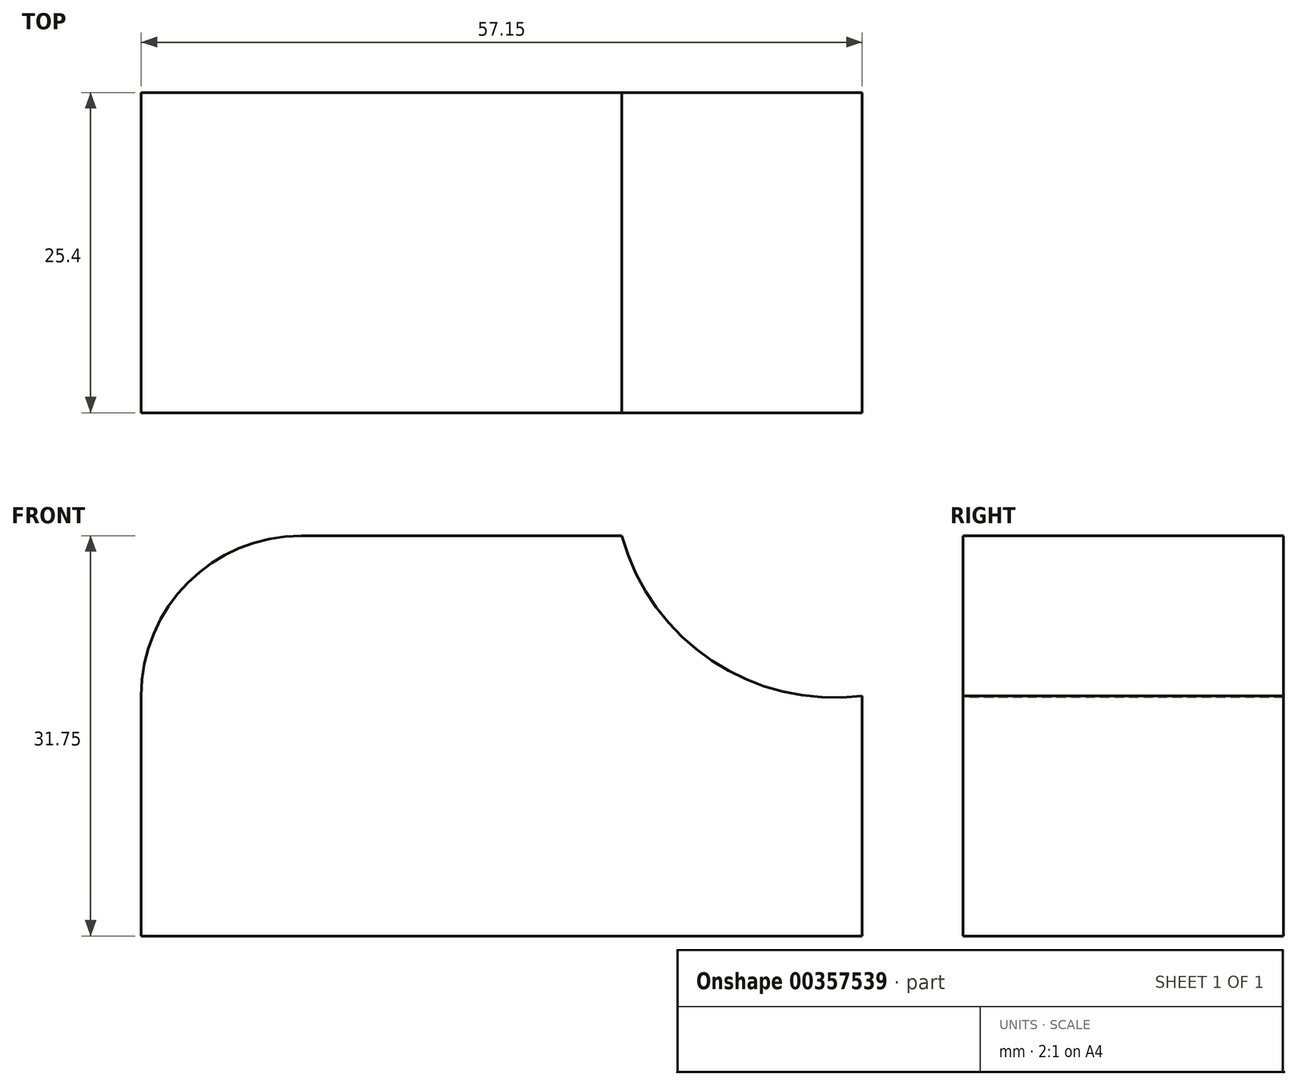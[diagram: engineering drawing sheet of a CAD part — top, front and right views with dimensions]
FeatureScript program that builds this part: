
annotation { "Feature Type Name" : "Feature", "Feature Type Description" : "" }
export const myFeature = defineFeature(function(context is Context, id is Id, definition is map)
    precondition{}
    {
        {
            var Q0;
            Q0=qCreatedBy(makeId("Front.planeOp"),FACE);
            var sketch = newSketch(context, id + "F0", { "sketchPlane" : qUnion([Q0])});
            skLineSegment(sketch, "E0.bottom", {"start": v(-36, 41.78) * mm, "end": v(21.15, 41.78) * mm});
            skLineSegment(sketch, "E0.top", {"start": v(-36, 10.03) * mm, "end": v(21.15, 10.03) * mm});
            skLineSegment(sketch, "E0.left", {"start": v(-36, 41.78) * mm, "end": v(-36, 10.03) * mm});
            skLineSegment(sketch, "E0.right", {"start": v(21.15, 41.78) * mm, "end": v(21.15, 10.03) * mm});
            skSolve(sketch);
        }
        {
            var Q0;
            Q0=makeQuery(id+"F0.imprint","IMPRINT",FACE,{"disambiguationData":[TD([[makeQuery(id+"F0.imprint","IMPRINT",EDGE,{"derivedFrom":sQuery(id+"F0.wireOp",EDGE,"E0.bottom")}),-1.0]])]});
            extrude(context, id + "F1", {"entities" : qUnion([Q0]), "depth" : 25.4 * mm});
        }
        {
            var Q0;
            Q0=makeQuery(id+"F1.opExtrude","CAP_FACE",FACE,{"disambiguationData":[OSD([sQuery(id+"F0.wireOp",EDGE,"E0.bottom"),sQuery(id+"F0.wireOp",EDGE,"E0.top"),sQuery(id+"F0.wireOp",EDGE,"E0.left"),sQuery(id+"F0.wireOp",EDGE,"E0.right")])],"isStart":false});
            var sketch = newSketch(context, id + "F2", { "sketchPlane" : qUnion([Q0])});
            skLineSegment(sketch, "E1", {"start": v(21.15, 10.03) * mm, "end": v(21.15, 29.08) * mm});
            skLineSegment(sketch, "E2", {"start": v(-36, 41.78) * mm, "end": v(2.1, 41.78) * mm});
            skPoint(sketch, "E3.third.point", {"position": v(28.79, 36.06) * mm});
            skArc(sketch, "E4", {"start": v(2.1, 41.78) * mm, "mid": v(9.25, 31.87) * mm, "end": v(21.15, 29.08) * mm});
            skSolve(sketch);
        }
        {
            var Q0;
            {var subQ1=makeQuery(id+"F1.opExtrude","CAP_EDGE",EDGE,{"disambiguationData":[OSD([sQuery(id+"F0.wireOp",EDGE,"E0.right")])],"isStart":false});var subQ3=makeQuery(id+"F1.opExtrude","CAP_EDGE",EDGE,{"disambiguationData":[OSD([sQuery(id+"F0.wireOp",EDGE,"E0.bottom")])],"isStart":false});var subQ5=makeQuery(id+"F2.imprint","INTERSECT",VERTEX,{"derivedFrom":[subQ3,subQ1]});Q0=makeQuery(id+"F2.imprint","IMPRINT",FACE,{"disambiguationData":[TD([[makeQuery(id+"F2.imprint","IMPRINT",EDGE,{"disambiguationData":[TD([[subQ5,1.0]])],"derivedFrom":subQ3}),-1.0]])]});}
            extrude(context, id + "F3", {"entities" : qUnion([Q0]), "operationType" : NewBodyOperationType.REMOVE, "oppositeDirection" : true, "depth" : 25.4 * mm});
        }
        {
            var Q0;
            Q0=makeQuery(id+"F1.opExtrude","CAP_FACE",FACE,{"disambiguationData":[OSD([sQuery(id+"F0.wireOp",EDGE,"E0.bottom"),sQuery(id+"F0.wireOp",EDGE,"E0.top"),sQuery(id+"F0.wireOp",EDGE,"E0.left"),sQuery(id+"F0.wireOp",EDGE,"E0.right")])],"isStart":false});
            var sketch = newSketch(context, id + "F4", { "sketchPlane" : qUnion([Q0])});
            skLineSegment(sketch, "E5", {"start": v(-36, 35.43) * mm, "end": v(-36, 10.03) * mm});
            skLineSegment(sketch, "E6", {"start": v(-23.3, 41.78) * mm, "end": v(2.1, 41.78) * mm});
            skLineSegment(sketch, "E7", {"start": v(2.1, 41.78) * mm, "end": v(-23.3, 41.78) * mm});
            skLineSegment(sketch, "E8", {"start": v(-36, 29.08) * mm, "end": v(-36, 10.03) * mm});
            skPoint(sketch, "E9.visualSharp", {"position": v(-36, 41.78) * mm});
            skArc(sketch, "E9.filletArc", {"start": v(-23.3, 41.78) * mm, "mid": v(-32.28, 38.06) * mm, "end": v(-36, 29.08) * mm});
            skSolve(sketch);
        }
        {
            var Q0;
            {var subQ0=sQuery(id+"F4.wireOp",EDGE,"E5");Q0=makeQuery(id+"F4.imprint","IMPRINT",FACE,{"disambiguationData":[TD([[makeQuery(id+"F4.imprint","IMPRINT",EDGE,{"derivedFrom":subQ0}),1.0]])]});}
            extrude(context, id + "F5", {"entities" : qUnion([Q0]), "operationType" : NewBodyOperationType.REMOVE, "oppositeDirection" : true, "depth" : 25.4 * mm});
        }
    });
